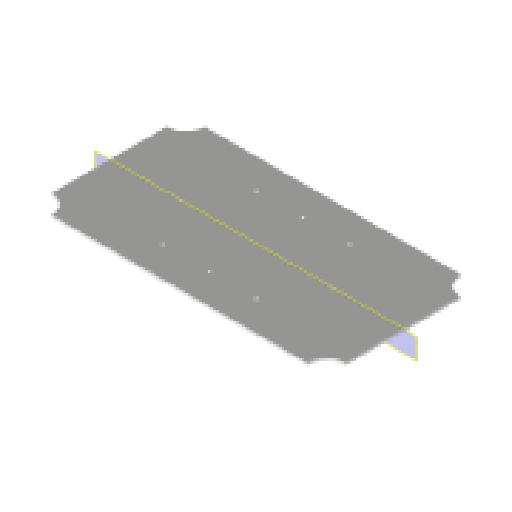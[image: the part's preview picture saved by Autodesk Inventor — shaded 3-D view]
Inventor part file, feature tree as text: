
AUTODESK INVENTOR PART (.ipt)
format: ipt  version: 2024.1 (Build 281209000, 209)  size: 154,624 bytes
history: native  units: mm
features: sketch x3, extrude x2, plane x2, projected_geometry x2, hole x1
ambient origin geometry x8: Origin, YZ Plane, XZ Plane, XY Plane, X Axis, Y Axis, Z Axis, Center Point
bodies: Volumenkörper1 (feature_tree)
feature tree (10):
  extrude  "Extrusion1"  Depth=120.0mm
  hole  "Bohrung1"  [1 undecoded]
  extrude  "Extrusion2"  Depth=10.0mm
  plane  "Arbeitsebene1"
  plane  "Arbeitsebene2"
  sketch  "Skizze1"  dims[d0=230.0mm d1=120.0mm]
  sketch  "Skizze2"  dims[d2=30.0mm d3=30.0mm]
  sketch  "Skizze3"  dims[d4=30.0mm d5=30.0mm d6=2.0mm d7=0.0mm d8=73.0mm d9=73.0mm d10=2.8mm d11=6.0mm d12=4.0mm d13=2.0mm d14=90.0deg d15=8.0mm d16=20.594885mm d17=10.0mm d18=10.0mm d19=10.0mm d20=10.0mm d21=10.0mm d22=10.0mm d23=13.5mm d24=0.0mm d25=23.5mm d26=23.5mm d27=10.0mm d28=10.0mm]
  projected_geometry  "Projizierte Kontur1"
  projected_geometry  "Projizierte Kontur2"
note: 1 required parameter value undecoded (feature->parameter linkage not recoverable at this tier; creation-order binding heuristic only, values carry confidence <= 0.55)
